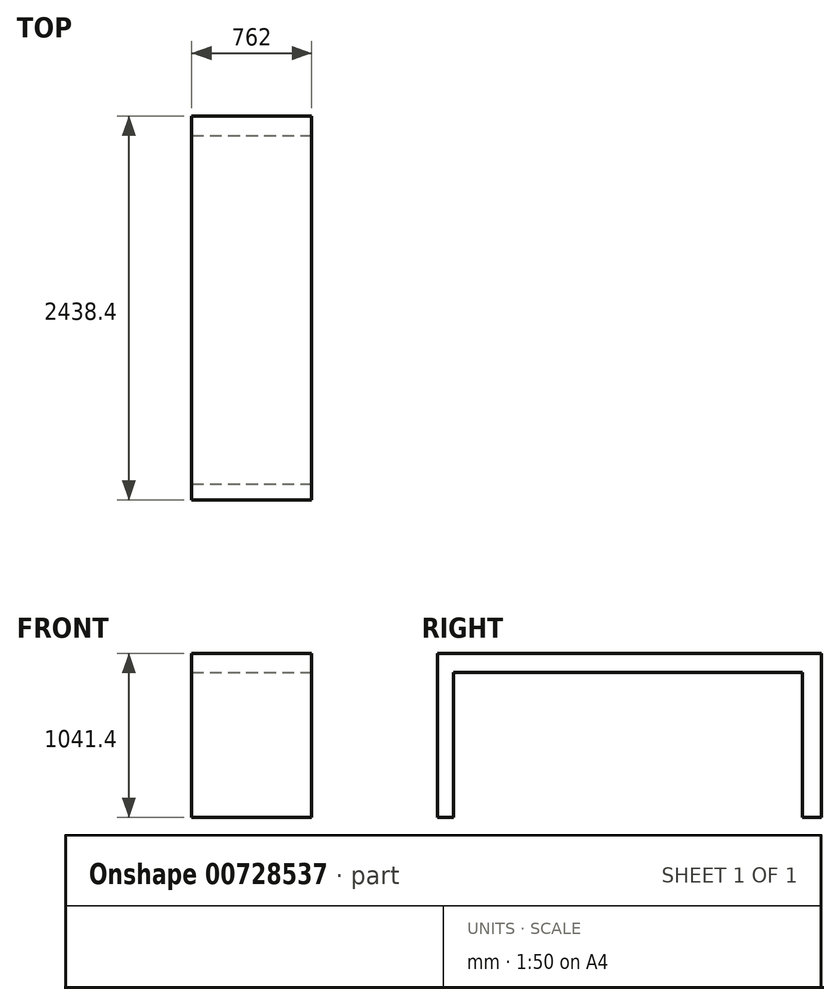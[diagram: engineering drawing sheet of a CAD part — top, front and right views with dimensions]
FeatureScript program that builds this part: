
annotation { "Feature Type Name" : "Feature", "Feature Type Description" : "" }
export const myFeature = defineFeature(function(context is Context, id is Id, definition is map)
    precondition{}
    {
        {
            var Q0;
            Q0=qCreatedBy(makeId("Top.planeOp"),FACE);
            var sketch = newSketch(context, id + "F0", { "sketchPlane" : qUnion([Q0])});
            skLineSegment(sketch, "E0.bottom", {"start": v(381, 1219.2) * mm, "end": v(-381, 1219.2) * mm});
            skLineSegment(sketch, "E0.top", {"start": v(381, -1219.2) * mm, "end": v(-381, -1219.2) * mm});
            skLineSegment(sketch, "E0.left", {"start": v(381, 1219.2) * mm, "end": v(381, -1219.2) * mm});
            skLineSegment(sketch, "E0.right", {"start": v(-381, 1219.2) * mm, "end": v(-381, -1219.2) * mm});
            skPoint(sketch, "E0.middle", {"position": v(0, 0) * mm});
            skSolve(sketch);
        }
        {
            var Q0;
            Q0 = qSketchRegion(id + "F0", true);
            extrude(context, id + "F1", {"entities" : qUnion([Q0]), "depth" : 1041.4 * mm, "offsetDistance" : 25.4 * mm});
        }
        {
            var Q0;
            Q0=makeQuery(id+"F1.opExtrude","SWEPT_FACE",FACE,{"disambiguationData":[OSD([sQuery(id+"F0.wireOp",EDGE,"E0.left")])]});
            var sketch = newSketch(context, id + "F2", { "sketchPlane" : qUnion([Q0])});
            skLineSegment(sketch, "E1.bottom", {"start": v(-1118.65, 0) * mm, "end": v(1096.52, 0) * mm});
            skLineSegment(sketch, "E1.top", {"start": v(-1118.65, 921.17) * mm, "end": v(1096.52, 921.17) * mm});
            skLineSegment(sketch, "E1.left", {"start": v(-1118.65, 0) * mm, "end": v(-1118.65, 921.17) * mm});
            skLineSegment(sketch, "E1.right", {"start": v(1096.52, 0) * mm, "end": v(1096.52, 921.17) * mm});
            skSolve(sketch);
        }
        {
            var Q0;
            Q0 = qSketchRegion(id + "F2", true);
            extrude(context, id + "F3", {"entities" : qUnion([Q0]), "operationType" : NewBodyOperationType.REMOVE, "endBound" : BoundingType.THROUGH_ALL, "oppositeDirection" : true, "depth" : 25.4 * mm, "offsetDistance" : 25.4 * mm});
        }
    });
